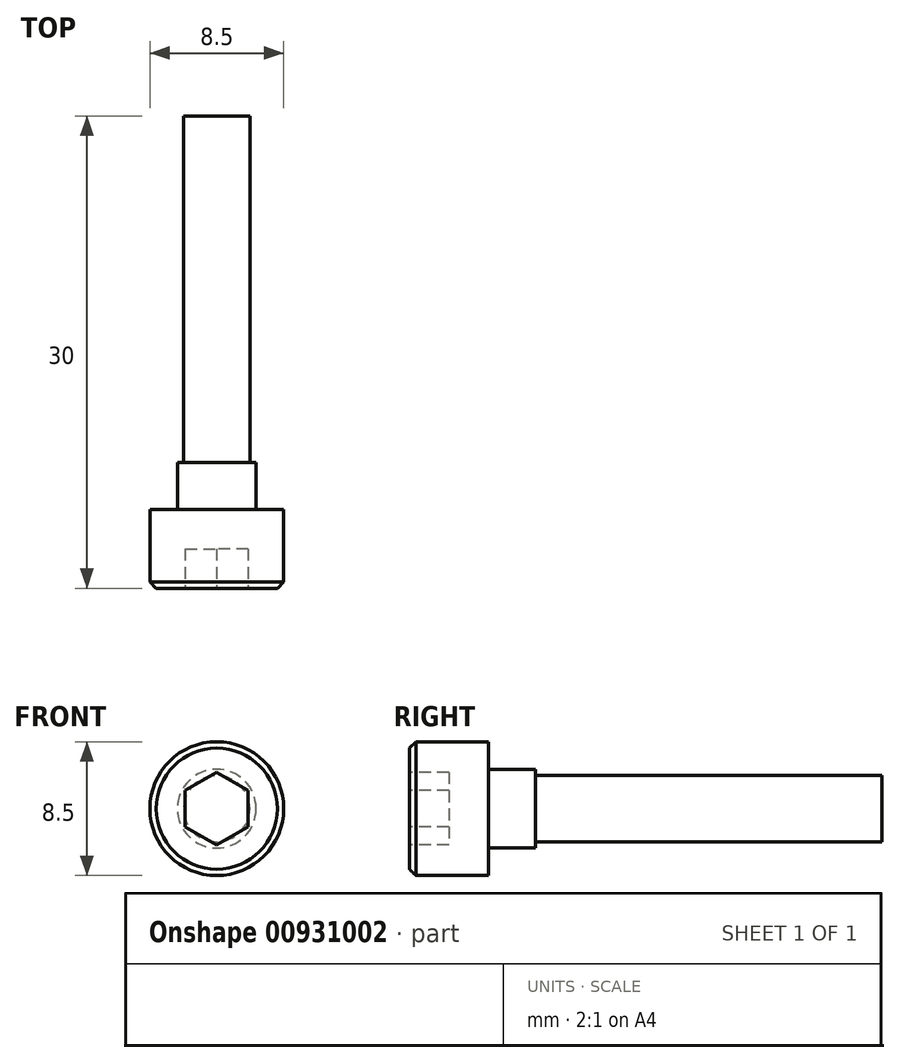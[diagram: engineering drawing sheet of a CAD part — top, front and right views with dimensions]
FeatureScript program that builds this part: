
annotation { "Feature Type Name" : "Feature", "Feature Type Description" : "" }
export const myFeature = defineFeature(function(context is Context, id is Id, definition is map)
    precondition{}
    {
        {
            var Q0;
            Q0=qCreatedBy(makeId("Front.planeOp"),FACE);
            var sketch = newSketch(context, id + "F0", { "sketchPlane" : qUnion([Q0])});
            skCircle(sketch, "E0", {"center": v(0, 0) * mm, "radius": 4.25 * mm});
            skSolve(sketch);
        }
        {
            var Q0;
            Q0=makeQuery(id+"F0.imprint","IMPRINT",FACE,{"disambiguationData":[TD([[makeQuery(id+"F0.imprint","IMPRINT",EDGE,{"derivedFrom":sQuery(id+"F0.wireOp",EDGE,"E0")}),1.0]])]});
            extrude(context, id + "F1", {"entities" : qUnion([Q0]), "depth" : 5 * mm, "offsetDistance" : 25 * mm});
        }
        {
            var Q0;
            Q0=makeQuery(id+"F1.opExtrude","CAP_FACE",FACE,{"disambiguationData":[OSD([sQuery(id+"F0.wireOp",EDGE,"E0")])],"isStart":true});
            var sketch = newSketch(context, id + "F2", { "sketchPlane" : qUnion([Q0])});
            skCircle(sketch, "E1", {"center": v(0, 0) * mm, "radius": 2.5 * mm});
            skSolve(sketch);
        }
        {
            var Q0;
            Q0=makeQuery(id+"F2.imprint","IMPRINT",FACE,{"disambiguationData":[TD([[makeQuery(id+"F2.imprint","IMPRINT",EDGE,{"derivedFrom":sQuery(id+"F2.wireOp",EDGE,"E1")}),1.0]])]});
            extrude(context, id + "F3", {"entities" : qUnion([Q0]), "operationType" : NewBodyOperationType.ADD, "depth" : 25 * mm, "offsetDistance" : 25 * mm});
        }
        {
            var Q0;
            Q0=makeQuery(id+"F3.opExtrude","CAP_FACE",FACE,{"disambiguationData":[OSD([sQuery(id+"F2.wireOp",EDGE,"E1")])],"isStart":false});
            var sketch = newSketch(context, id + "F4", { "sketchPlane" : qUnion([Q0])});
            skCircle(sketch, "E2", {"center": v(0, 0) * mm, "radius": 2.1 * mm});
            skSolve(sketch);
        }
        {
            var Q0;
            Q0=makeQuery(id+"F4.imprint","IMPRINT",FACE,{"disambiguationData":[TD([[makeQuery(id+"F4.imprint","IMPRINT",EDGE,{"derivedFrom":sQuery(id+"F4.wireOp",EDGE,"E2")}),-1.0]])]});
            extrude(context, id + "F5", {"entities" : qUnion([Q0]), "operationType" : NewBodyOperationType.REMOVE, "oppositeDirection" : true, "depth" : 22 * mm, "offsetDistance" : 25 * mm});
        }
        {
            var Q0;
            Q0=makeQuery(id+"F1.opExtrude","CAP_FACE",FACE,{"disambiguationData":[OSD([sQuery(id+"F0.wireOp",EDGE,"E0")])],"isStart":false});
            var sketch = newSketch(context, id + "F6", { "sketchPlane" : qUnion([Q0])});
            skCircle(sketch, "E3.cCircle", {"center": v(0, 0) * mm, "radius": 2 * mm, "construction": true});
            skLineSegment(sketch, "E3.0", {"start": v(2, -1.15) * mm, "end": v(0, -2.3) * mm});
            skLineSegment(sketch, "E3.1", {"start": v(0, -2.3) * mm, "end": v(-2, -1.15) * mm});
            skLineSegment(sketch, "E3.2", {"start": v(-2, -1.15) * mm, "end": v(-2, 1.15) * mm});
            skLineSegment(sketch, "E3.3", {"start": v(-2, 1.15) * mm, "end": v(0, 2.3) * mm});
            skLineSegment(sketch, "E3.4", {"start": v(0, 2.3) * mm, "end": v(2, 1.15) * mm});
            skLineSegment(sketch, "E3.5", {"start": v(2, 1.15) * mm, "end": v(2, -1.15) * mm});
            skPoint(sketch, "E3.0.midPoint", {"position": v(1, -1.73) * mm});
            skLineSegment(sketch, "E4", {"start": v(0, 0) * mm, "end": v(4.25, 0) * mm, "construction": true});
            skSolve(sketch);
        }
        {
            var Q0;
            Q0 = qSketchRegion(id + "F6", true);
            extrude(context, id + "F7", {"entities" : qUnion([Q0]), "operationType" : NewBodyOperationType.REMOVE, "oppositeDirection" : true, "depth" : 2.5 * mm, "offsetDistance" : 25 * mm});
        }
        {
            var Q0;
            Q0=makeQuery(id+"F1.opExtrude","CAP_EDGE",EDGE,{"disambiguationData":[OSD([sQuery(id+"F0.wireOp",EDGE,"E0")])],"isStart":false});
            chamfer(context, id + "F8", {"entities" : qUnion([Q0]), "width" : 0.4 * mm, "tangentPropagation" : true});
        }
    });
